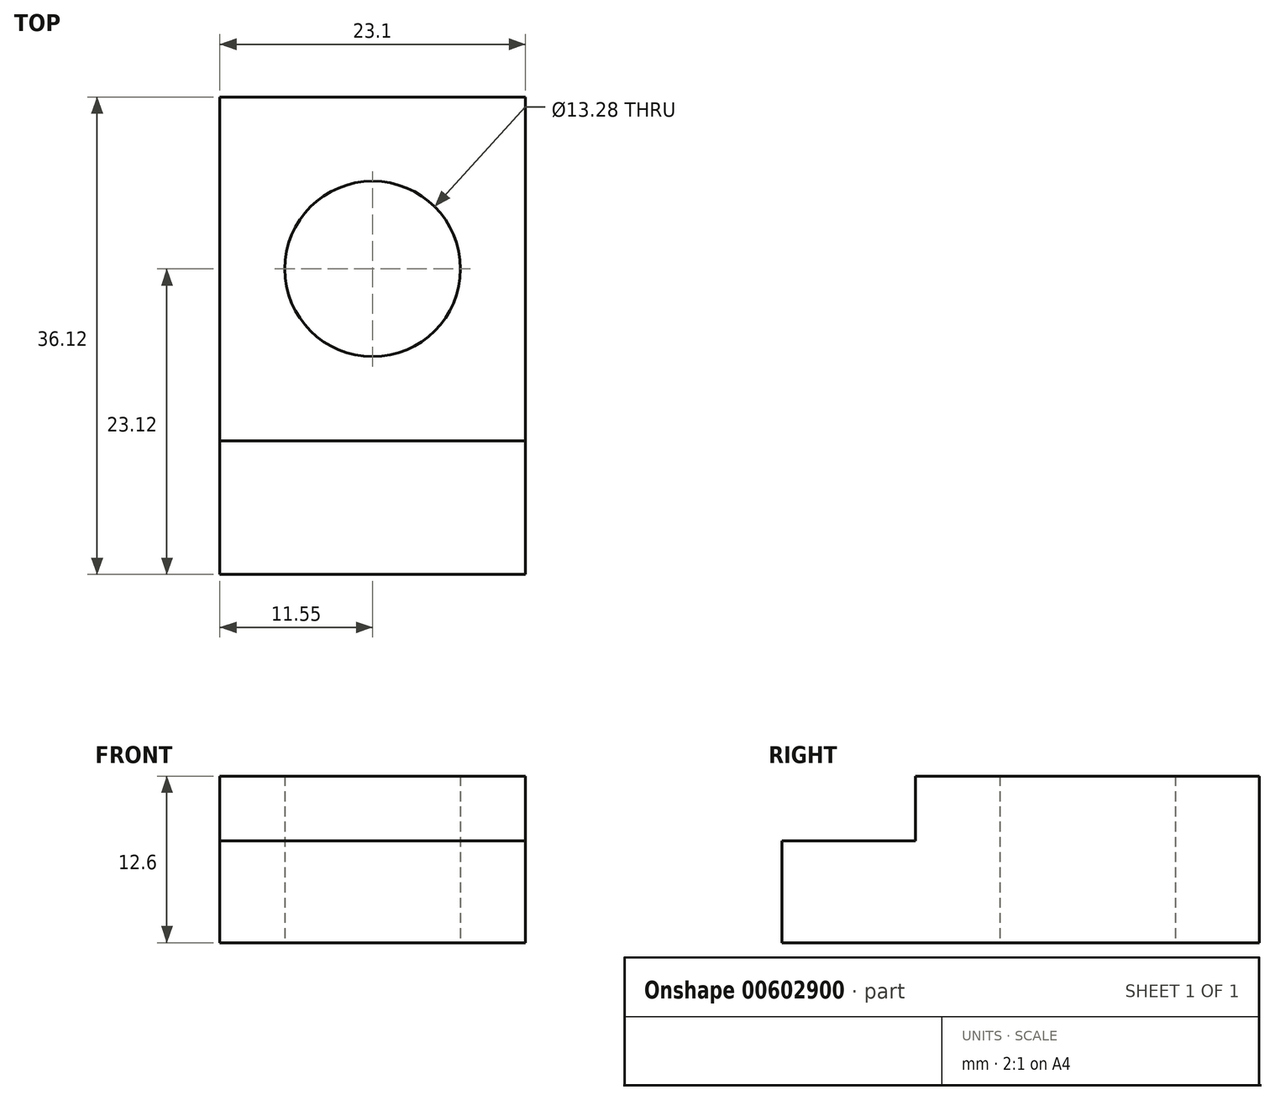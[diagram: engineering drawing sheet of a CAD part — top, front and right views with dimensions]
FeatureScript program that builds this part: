
annotation { "Feature Type Name" : "Feature", "Feature Type Description" : "" }
export const myFeature = defineFeature(function(context is Context, id is Id, definition is map)
    precondition{}
    {
        {
            var Q0;
            Q0=qCreatedBy(makeId("Top.planeOp"),FACE);
            var sketch = newSketch(context, id + "F0", { "sketchPlane" : qUnion([Q0])});
            skLineSegment(sketch, "E0.bottom", {"start": v(-11.55, 18.06) * mm, "end": v(11.55, 18.06) * mm});
            skLineSegment(sketch, "E0.top", {"start": v(-11.55, -18.06) * mm, "end": v(11.55, -18.06) * mm});
            skLineSegment(sketch, "E0.left", {"start": v(-11.55, 18.06) * mm, "end": v(-11.55, -18.06) * mm});
            skLineSegment(sketch, "E0.right", {"start": v(11.55, 18.06) * mm, "end": v(11.55, -18.06) * mm});
            skPoint(sketch, "E0.middle", {"position": v(0, 0) * mm});
            skSolve(sketch);
        }
        {
            var Q0;
            Q0=qCreatedBy(makeId("Top.planeOp"),FACE);
            var sketch = newSketch(context, id + "F1", { "sketchPlane" : qUnion([Q0])});
            skLineSegment(sketch, "E1.bottom", {"start": v(-11.55, 18.06) * mm, "end": v(11.55, 18.06) * mm});
            skLineSegment(sketch, "E1.top", {"start": v(-11.55, -7.94) * mm, "end": v(11.55, -7.94) * mm});
            skLineSegment(sketch, "E1.left", {"start": v(-11.55, 18.06) * mm, "end": v(-11.55, -7.94) * mm});
            skLineSegment(sketch, "E1.right", {"start": v(11.55, 18.06) * mm, "end": v(11.55, -7.94) * mm});
            skSolve(sketch);
        }
        {
            var Q0;
            Q0 = qSketchRegion(id + "F0", true);
            extrude(context, id + "F2", {"entities" : qUnion([Q0]), "depth" : 7.7 * mm, "offsetDistance" : 25 * mm});
        }
        {
            var Q0;
            Q0 = qSketchRegion(id + "F1", true);
            extrude(context, id + "F3", {"entities" : qUnion([Q0]), "operationType" : NewBodyOperationType.ADD, "depth" : 12.6 * mm, "offsetDistance" : 25 * mm});
        }
        {
            var Q0;
            Q0=qCreatedBy(makeId("Top.planeOp"),FACE);
            var sketch = newSketch(context, id + "F4", { "sketchPlane" : qUnion([Q0])});
            skCircle(sketch, "E2", {"center": v(0, 5.06) * mm, "radius": 6.64 * mm});
            skSolve(sketch);
        }
        {
            var Q0;
            Q0 = qSketchRegion(id + "F4", true);
            extrude(context, id + "F5", {"entities" : qUnion([Q0]), "operationType" : NewBodyOperationType.REMOVE, "depth" : 12.6 * mm, "offsetDistance" : 25 * mm});
        }
    });
